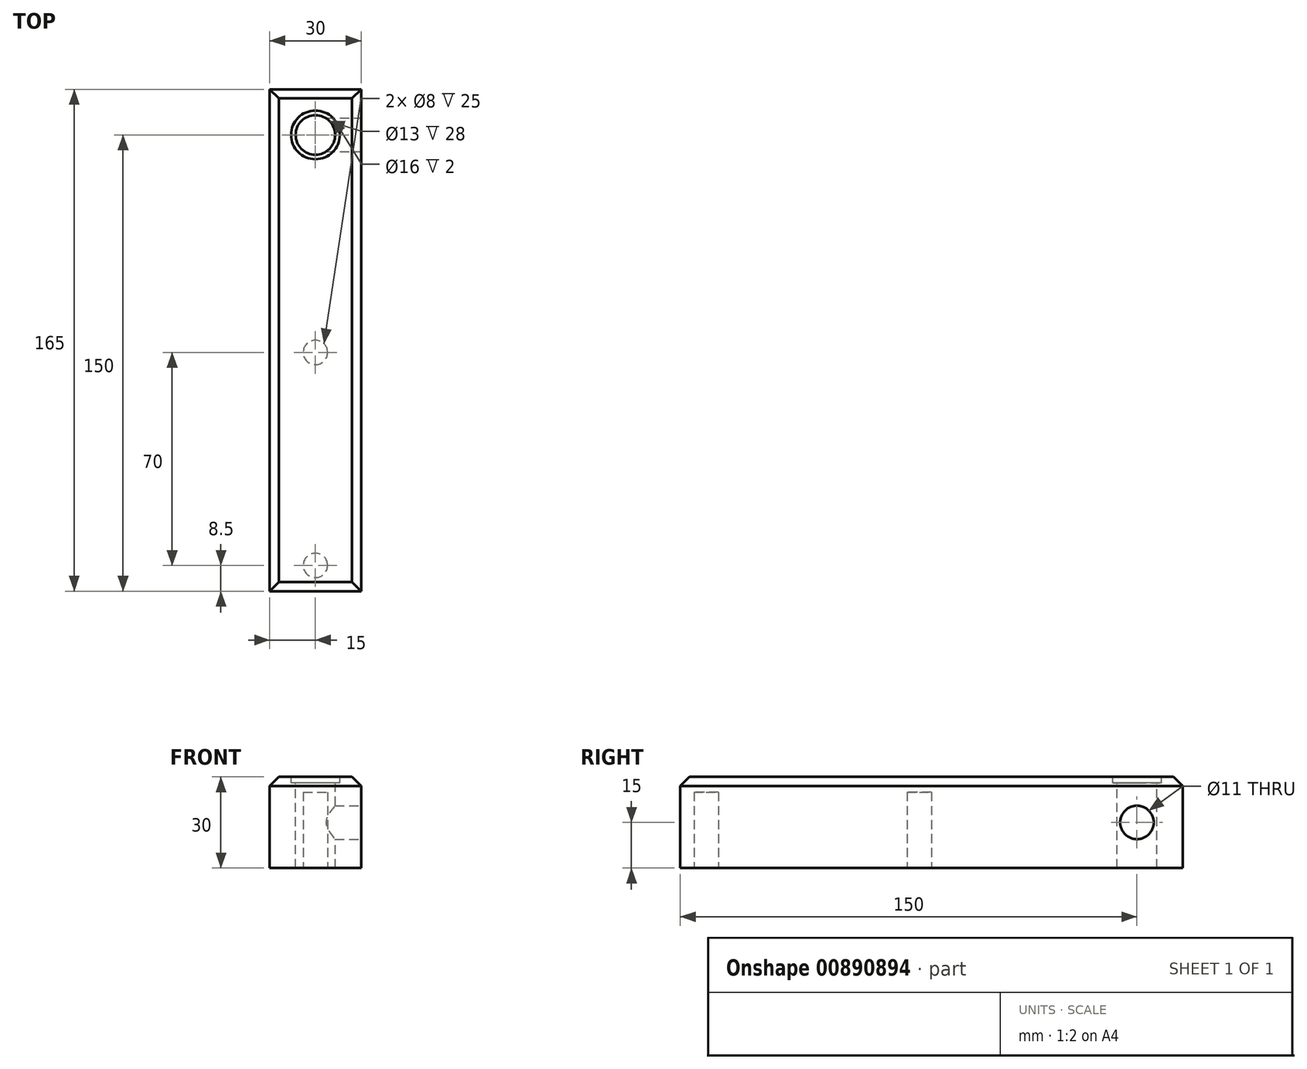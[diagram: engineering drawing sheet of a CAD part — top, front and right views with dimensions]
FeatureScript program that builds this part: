
annotation { "Feature Type Name" : "Feature", "Feature Type Description" : "" }
export const myFeature = defineFeature(function(context is Context, id is Id, definition is map)
    precondition{}
    {
        {
            var Q0;
            Q0=qCreatedBy(makeId("Front.planeOp"),FACE);
            var sketch = newSketch(context, id + "F0", { "sketchPlane" : qUnion([Q0])});
            skLineSegment(sketch, "E0.bottom", {"start": v(-15, -15) * mm, "end": v(15, -15) * mm});
            skLineSegment(sketch, "E0.top", {"start": v(-15, 15) * mm, "end": v(15, 15) * mm});
            skLineSegment(sketch, "E0.left", {"start": v(-15, -15) * mm, "end": v(-15, 15) * mm});
            skLineSegment(sketch, "E0.right", {"start": v(15, -15) * mm, "end": v(15, 15) * mm});
            skPoint(sketch, "E0.middle", {"position": v(0, 0) * mm});
            skSolve(sketch);
        }
        {
            var Q0;
            Q0=makeQuery(id+"F0.imprint","IMPRINT",FACE,{"disambiguationData":[TD([[makeQuery(id+"F0.imprint","IMPRINT",EDGE,{"derivedFrom":sQuery(id+"F0.wireOp",EDGE,"E0.bottom")}),1.0]])]});
            extrude(context, id + "F1", {"entities" : qUnion([Q0]), "depth" : 165 * mm, "offsetDistance" : 25 * mm});
        }
        {
            var Q0;
            Q0=makeQuery(id+"F1.opExtrude","SWEPT_FACE",FACE,{"disambiguationData":[OSD([sQuery(id+"F0.wireOp",EDGE,"E0.top")])]});
            var sketch = newSketch(context, id + "F2", { "sketchPlane" : qUnion([Q0])});
            skLineSegment(sketch, "E1", {"start": v(0, 0) * mm, "end": v(0, -15) * mm});
            skCircle(sketch, "E2", {"center": v(0, -15) * mm, "radius": 6.5 * mm});
            skSolve(sketch);
        }
        {
            var Q0;
            Q0 = qSketchRegion(id + "F2", true);
            extrude(context, id + "F3", {"entities" : qUnion([Q0]), "operationType" : NewBodyOperationType.REMOVE, "oppositeDirection" : true, "depth" : 30 * mm, "offsetDistance" : 25 * mm});
        }
        {
            var Q0;
            Q0=makeQuery(id+"F1.opExtrude","SWEPT_FACE",FACE,{"disambiguationData":[OSD([sQuery(id+"F0.wireOp",EDGE,"E0.right")])]});
            var sketch = newSketch(context, id + "F4", { "sketchPlane" : qUnion([Q0])});
            skLineSegment(sketch, "E3", {"start": v(-15, 0) * mm, "end": v(0, 0) * mm});
            skCircle(sketch, "E4", {"center": v(-15, 0) * mm, "radius": 5.5 * mm});
            skSolve(sketch);
        }
        {
            var Q0;
            Q0 = qSketchRegion(id + "F4", true);
            extrude(context, id + "F5", {"entities" : qUnion([Q0]), "operationType" : NewBodyOperationType.REMOVE, "oppositeDirection" : true, "depth" : 12.3 * mm, "offsetDistance" : 25 * mm});
        }
        {
            var Q0;
            Q0=makeQuery(id+"F1.opExtrude","SWEPT_FACE",FACE,{"disambiguationData":[OSD([sQuery(id+"F0.wireOp",EDGE,"E0.top")])]});
            var sketch = newSketch(context, id + "F6", { "sketchPlane" : qUnion([Q0])});
            skCircle(sketch, "E5", {"center": v(0, -15) * mm, "radius": 8 * mm});
            skSolve(sketch);
        }
        {
            var Q0;
            Q0=makeQuery(id+"F6.imprint","IMPRINT",FACE,{"disambiguationData":[TD([[makeQuery(id+"F6.imprint","IMPRINT",EDGE,{"derivedFrom":makeQuery(id+"F3.boolean.opBoolean","COPY",EDGE,{"derivedFrom":makeQuery(id+"F3.opExtrude","CAP_EDGE",EDGE,{"disambiguationData":[OSD([sQuery(id+"F2.wireOp",EDGE,"E2")])],"isStart":true})})}),1.0]])]});
            var Q1;
            Q1=makeQuery(id+"F6.imprint","IMPRINT",FACE,{"disambiguationData":[TD([[makeQuery(id+"F6.imprint","IMPRINT",EDGE,{"derivedFrom":sQuery(id+"F6.wireOp",EDGE,"E5")}),1.0]])]});
            extrude(context, id + "F7", {"entities" : qUnion([Q0, Q1]), "operationType" : NewBodyOperationType.REMOVE, "oppositeDirection" : true, "depth" : 2 * mm, "offsetDistance" : 25 * mm});
        }
        {
            var Q0;
            Q0=makeQuery(id+"F1.opExtrude","SWEPT_EDGE",EDGE,{"disambiguationData":[OSD([sQuery(id+"F0.wireOp",EDGE,"E0.top"),sQuery(id+"F0.wireOp",EDGE,"E0.right")])]});
            var Q1;
            Q1=makeQuery(id+"F1.opExtrude","CAP_EDGE",EDGE,{"disambiguationData":[OSD([sQuery(id+"F0.wireOp",EDGE,"E0.top")])],"isStart":true});
            var Q2;
            Q2=makeQuery(id+"F1.opExtrude","SWEPT_EDGE",EDGE,{"disambiguationData":[OSD([sQuery(id+"F0.wireOp",EDGE,"E0.top"),sQuery(id+"F0.wireOp",EDGE,"E0.left")])]});
            var Q3;
            Q3=makeQuery(id+"F1.opExtrude","CAP_EDGE",EDGE,{"disambiguationData":[OSD([sQuery(id+"F0.wireOp",EDGE,"E0.top")])],"isStart":false});
            chamfer(context, id + "F8", {"entities" : qUnion([Q0, Q1, Q2, Q3]), "width" : 3 * mm, "tangentPropagation" : true});
        }
        {
            var Q0;
            Q0=makeQuery(id+"F1.opExtrude","SWEPT_FACE",FACE,{"disambiguationData":[OSD([sQuery(id+"F0.wireOp",EDGE,"E0.bottom")])]});
            var sketch = newSketch(context, id + "F9", { "sketchPlane" : qUnion([Q0])});
            skLineSegment(sketch, "E6", {"start": v(0, 0) * mm, "end": v(0, 86.5) * mm});
            skPoint(sketch, "E6.endSnap0", {"position": v(0, 165) * mm});
            skLineSegment(sketch, "E7", {"start": v(0, 86.5) * mm, "end": v(0, 156.5) * mm});
            skCircle(sketch, "E8", {"center": v(0, 156.5) * mm, "radius": 4 * mm});
            skCircle(sketch, "E9", {"center": v(0, 86.5) * mm, "radius": 4 * mm});
            skSolve(sketch);
        }
        {
            var Q0;
            {var subQ0=sQuery(id+"F9.wireOp",EDGE,"E7");var subQ1=sQuery(id+"F9.wireOp",EDGE,"E6");var subQ2=makeQuery(id+"F9.imprint","INTERSECT",VERTEX,{"derivedFrom":[subQ1,subQ0]});Q0=makeQuery(id+"F9.imprint","IMPRINT",FACE,{"disambiguationData":[TD([[makeQuery(id+"F9.imprint","IMPRINT",EDGE,{"disambiguationData":[TD([[subQ2,1.0]])],"derivedFrom":subQ1}),1.0]])]});}
            var Q1;
            {var subQ0=sQuery(id+"F9.wireOp",EDGE,"E7");var subQ1=sQuery(id+"F9.wireOp",EDGE,"E6");var subQ2=makeQuery(id+"F9.imprint","INTERSECT",VERTEX,{"derivedFrom":[subQ1,subQ0]});Q1=makeQuery(id+"F9.imprint","IMPRINT",FACE,{"disambiguationData":[TD([[makeQuery(id+"F9.imprint","IMPRINT",EDGE,{"disambiguationData":[TD([[subQ2,1.0]])],"derivedFrom":subQ1}),-1.0]])]});}
            var Q2;
            Q2=makeQuery(id+"F9.imprint","IMPRINT",FACE,{"disambiguationData":[TD([[makeQuery(id+"F9.imprint","IMPRINT",EDGE,{"derivedFrom":sQuery(id+"F9.wireOp",EDGE,"E8")}),1.0]])]});
            extrude(context, id + "F10", {"entities" : qUnion([Q0, Q1, Q2]), "operationType" : NewBodyOperationType.REMOVE, "oppositeDirection" : true, "depth" : 25 * mm, "offsetDistance" : 25 * mm});
        }
    });
